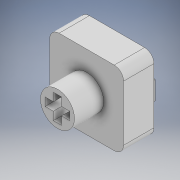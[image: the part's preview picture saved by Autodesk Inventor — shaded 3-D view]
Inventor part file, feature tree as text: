
AUTODESK INVENTOR PART (.ipt)
format: ipt  version: 2022 (Build 260153000, 153)  size: 215,552 bytes
history: native  units: in
note: dims shown in document units (in); Inventor stores cm internally (conversion verified against a paired STEP export)
features: sketch x4, extrude x3, plane x1, projected_geometry x1
ambient origin geometry x8: Origin, YZ Plane, XZ Plane, XY Plane, X Axis, Y Axis, Z Axis, Center Point
bodies: Body1 (feature_tree)
feature tree (9):
  sketch  "Sketch1"  dims[d3=0.2205in d4=0.1594in]
  plane  "Work Plane1"
  sketch  "Sketch2"  dims[d5=0.0531in d6=0.1594in]
  extrude  "Extrusion3"  Depth=0.1594in
  extrude  "Extrusion4"  Depth=0.1594in
  extrude  "Extrusion5"  Depth=0.5016in
  projected_geometry  "Projected Loop1"
  sketch  "Sketch3"  dims[d7=0.0531in d10=0.5016in]
  sketch  "Sketch4"  dims[d12=0.1969in d13=0.0in d14=0.2205in d15=0.1594in d16=0.0531in d17=0.1594in d18=0.0531in d19=0.189in d20=0.0in d21=0.0892in d22=0.2693in d23=0.0354in d24=0.0in]
